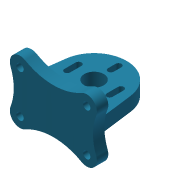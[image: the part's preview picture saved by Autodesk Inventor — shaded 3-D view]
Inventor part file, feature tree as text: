
AUTODESK INVENTOR PART (.ipt)
format: ipt  version: 2014 (Build 180170000, 170)  size: 212,992 bytes
history: native  units: mm
features: extrude x5, sketch x5
ambient origin geometry x8: Origin, YZ Plane, XZ Plane, XY Plane, X Axis, Y Axis, Z Axis, Center Point
bodies: Solid1 (feature_tree)
feature tree (10):
  extrude  "Extrusion1"  Depth=26.0mm
  extrude  "Extrusion2"  Depth=4.0mm
  extrude  "Extrusion3"  Depth=35.0mm
  extrude  "Extrusion4"  Depth=20.0mm
  extrude  "Extrusion5"  Depth=3.5mm
  sketch  "Sketch1"  dims[d0=26.0mm d1=41.0mm]
  sketch  "Sketch2"  dims[d2=4.5mm d3=4.0mm]
  sketch  "Sketch3"  dims[d4=30.0mm d5=35.0mm]
  sketch  "Sketch4"  dims[d6=7.0mm d7=0.0mm d8=20.0mm]
  sketch  "Sketch7"  dims[d9=18.0mm d10=45.0mm d11=8.5mm d12=0.0mm d13=12.0mm d14=7.5mm d15=0.0mm d16=3.6mm d17=4.75mm d18=2.5mm d19=2.5mm d20=13.0mm d21=13.0mm d22=7.0mm d23=7.5mm d24=0.0mm d25=5.75mm d26=3.5mm d27=0.0mm]
